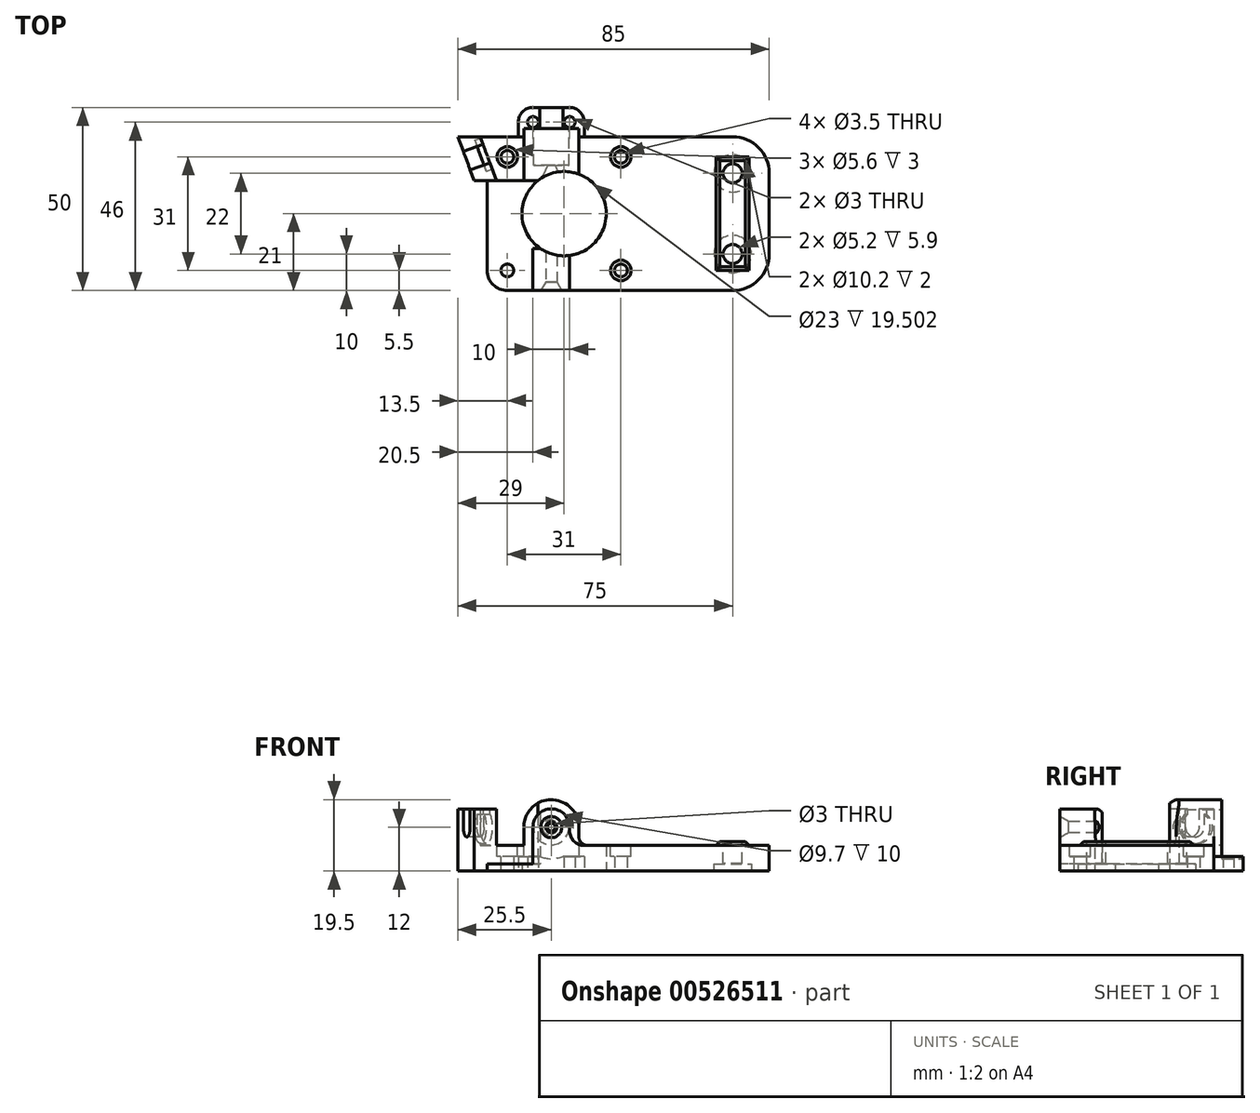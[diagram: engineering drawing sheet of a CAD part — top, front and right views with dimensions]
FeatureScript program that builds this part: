
annotation { "Feature Type Name" : "Feature", "Feature Type Description" : "" }
export const myFeature = defineFeature(function(context is Context, id is Id, definition is map)
    precondition{}
    {
        {
            var Q0;
            Q0=qCreatedBy(makeId("Top.planeOp"),FACE);
            var sketch = newSketch(context, id + "F0", { "sketchPlane" : qUnion([Q0])});
            skLineSegment(sketch, "E0.bottom", {"start": v(42.5, -21) * mm, "end": v(-34.5, -21) * mm});
            skLineSegment(sketch, "E0.top", {"start": v(42.5, 21) * mm, "end": v(-42.5, 21) * mm});
            skLineSegment(sketch, "E0.left", {"start": v(42.5, -21) * mm, "end": v(42.5, 21) * mm});
            skPoint(sketch, "E0.middle", {"position": v(0, 0) * mm});
            skLineSegment(sketch, "E1", {"start": v(-42.5, 21) * mm, "end": v(-38.06, 9) * mm});
            skLineSegment(sketch, "E2", {"start": v(-38.06, 9) * mm, "end": v(-34.5, 9) * mm});
            skLineSegment(sketch, "E3", {"start": v(-34.5, 9) * mm, "end": v(-34.5, -21) * mm});
            skPoint(sketch, "E4.orphan", {"position": v(-42.5, -21) * mm});
            skSolve(sketch);
        }
        {
            var Q0;
            Q0=makeQuery(id+"F0.imprint","IMPRINT",FACE,{"disambiguationData":[TD([[makeQuery(id+"F0.imprint","IMPRINT",EDGE,{"derivedFrom":sQuery(id+"F0.wireOp",EDGE,"E0.bottom")}),-1.0]])]});
            extrude(context, id + "F1", {"entities" : qUnion([Q0]), "depth" : 7 * mm, "offsetDistance" : 25 * mm});
        }
        {
            var Q0;
            Q0=makeQuery(id+"F1.opExtrude","SWEPT_FACE",FACE,{"disambiguationData":[OSD([sQuery(id+"F0.wireOp",EDGE,"E0.bottom")])]});
            var Q1;
            Q1=makeQuery(id+"F1.opExtrude","SWEPT_FACE",FACE,{"disambiguationData":[OSD([sQuery(id+"F0.wireOp",EDGE,"E0.top")])]});
            cPlane(context, id + "F2", {"entities" : qUnion([Q0, Q1]), "cplaneType" : CPlaneType.MID_PLANE, "offset" : 25 * mm, "width" : 150 * mm, "height" : 150 * mm});
        }
        {
            var Q0;
            Q0=makeQuery(id+"F1.opExtrude","SWEPT_FACE",FACE,{"disambiguationData":[OSD([sQuery(id+"F0.wireOp",EDGE,"E0.bottom")])]});
            var sketch = newSketch(context, id + "F3", { "sketchPlane" : qUnion([Q0])});
            skLineSegment(sketch, "E5", {"start": v(-22, 0) * mm, "end": v(-22, 12) * mm});
            skArc(sketch, "E6", {"start": v(-22, 12) * mm, "mid": v(-17, 17) * mm, "end": v(-12, 12) * mm});
            skLineSegment(sketch, "E7", {"start": v(-12, 12) * mm, "end": v(-12, 0) * mm});
            skLineSegment(sketch, "E8", {"start": v(-12, 0) * mm, "end": v(-22, 0) * mm});
            skSolve(sketch);
        }
        {
            var Q0;
            Q0 = qSketchRegion(id + "F3", true);
            var Q1;
            Q1=qCreatedBy(id+"F2.planeOp",FACE);
            extrude(context, id + "F4", {"entities" : qUnion([Q0]), "operationType" : NewBodyOperationType.ADD, "endBound" : BoundingType.UP_TO_SURFACE, "oppositeDirection" : true, "depth" : 25 * mm, "endBoundEntityFace" : qUnion([Q1]), "offsetDistance" : 25 * mm});
        }
        {
            var Q0;
            Q0=makeQuery(id+"F4.boolean.opBoolean","MERGE",FACE,{"derivedFrom":[makeQuery(id+"F1.opExtrude","SWEPT_FACE",FACE,{"disambiguationData":[OSD([sQuery(id+"F0.wireOp",EDGE,"E0.bottom")])]}),makeQuery(id+"F4.opExtrude","CAP_FACE",FACE,{"disambiguationData":[OSD([sQuery(id+"F3.wireOp",EDGE,"E5"),sQuery(id+"F3.wireOp",EDGE,"E6"),sQuery(id+"F3.wireOp",EDGE,"E7"),sQuery(id+"F3.wireOp",EDGE,"E8")])],"isStart":true})]});
            var sketch = newSketch(context, id + "F5", { "sketchPlane" : qUnion([Q0])});
            skPoint(sketch, "E9", {"position": v(-17, 12) * mm});
            skSolve(sketch);
        }
        {
            var Q0;
            Q0=sQuery(id+"F5.wireOp",VERTEX,"E9");
            var Q1;
            Q1=makeQuery(id+"F1.opExtrude","SWEPT_BODY",BODY,{"disambiguationData":[OSD([sQuery(id+"F0.wireOp",EDGE,"E0.bottom"),sQuery(id+"F0.wireOp",EDGE,"E0.top"),sQuery(id+"F0.wireOp",EDGE,"E0.left"),sQuery(id+"F0.wireOp",EDGE,"E1"),sQuery(id+"F0.wireOp",EDGE,"E2"),sQuery(id+"F0.wireOp",EDGE,"E3")])]});
            hole(context, id + "F6", {"style" : HoleStyle.C_SINK, "endStyle" : HoleEndStyle.THROUGH, "standardTappedOrClearance" : lookupTablePath({ "standard" : "ISO", "size" : "3", "type" : "Drilled" }), "standardBlindInLast" : lookupTablePath({ "standard" : "ISO", "size" : "3", "type" : "Drilled" }), "holeDiameter" : 3 * mm, "cSinkDiameter" : 5.76 * mm, "cSinkAngle" : 60 * degree, "isTappedThrough" : true, "tappedDepth" : 12 * mm, "tapClearance" : 3, "locations" : qUnion([Q0]), "scope" : qUnion([Q1])});
        }
        {
            var Q0;
            Q0=qCreatedBy(id+"F2.planeOp",FACE);
            var sketch = newSketch(context, id + "F7", { "sketchPlane" : qUnion([Q0])});
            skLineSegment(sketch, "E10", {"start": v(-24.5, 0) * mm, "end": v(-24.5, 12) * mm});
            skArc(sketch, "E11", {"start": v(-24.5, 12) * mm, "mid": v(-17, 19.5) * mm, "end": v(-9.5, 12) * mm});
            skLineSegment(sketch, "E12", {"start": v(-9.5, 12) * mm, "end": v(-9.5, 0) * mm});
            skLineSegment(sketch, "E13", {"start": v(-9.5, 0) * mm, "end": v(-24.5, 0) * mm});
            skSolve(sketch);
        }
        {
            var Q0;
            Q0=makeQuery(id+"F7.imprint","IMPRINT",FACE,{"disambiguationData":[TD([[makeQuery(id+"F7.imprint","IMPRINT",EDGE,{"derivedFrom":sQuery(id+"F7.wireOp",EDGE,"E10")}),-1.0]])]});
            var Q1;
            Q1=sQuery(id+"F7.wireOp",EDGE,"E11");
            extrude(context, id + "F8", {"entities" : qUnion([Q0]), "operationType" : NewBodyOperationType.ADD, "surfaceEntities" : qUnion([Q1]), "oppositeDirection" : true, "depth" : 23.2 * mm, "offsetDistance" : 25 * mm});
        }
        {
            var Q0;
            Q0=makeQuery(id+"F8.boolean.opBoolean","MERGE",FACE,{"derivedFrom":[makeQuery(id+"F1.opExtrude","CAP_FACE",FACE,{"disambiguationData":[OSD([sQuery(id+"F0.wireOp",EDGE,"E0.bottom"),sQuery(id+"F0.wireOp",EDGE,"E0.top"),sQuery(id+"F0.wireOp",EDGE,"E0.left"),sQuery(id+"F0.wireOp",EDGE,"E1"),sQuery(id+"F0.wireOp",EDGE,"E2"),sQuery(id+"F0.wireOp",EDGE,"E3")])],"isStart":true}),makeQuery(id+"F8.opExtrude","SWEPT_FACE",FACE,{"disambiguationData":[OSD([sQuery(id+"F7.wireOp",EDGE,"E13")])]})]});
            var sketch = newSketch(context, id + "F9", { "sketchPlane" : qUnion([Q0])});
            skLineSegment(sketch, "E14", {"start": v(-8, -21) * mm, "end": v(-8, -29) * mm});
            skLineSegment(sketch, "E15", {"start": v(-8, -29) * mm, "end": v(-26, -29) * mm});
            skLineSegment(sketch, "E16", {"start": v(-26, -29) * mm, "end": v(-26, -21) * mm});
            skLineSegment(sketch, "E17", {"start": v(-8, -21) * mm, "end": v(-26, -21) * mm});
            skCircle(sketch, "E18", {"center": v(-12, -25) * mm, "radius": 1.5 * mm});
            skCircle(sketch, "E19", {"center": v(-22, -25) * mm, "radius": 1.5 * mm});
            skLineSegment(sketch, "E20", {"start": v(-12, -25) * mm, "end": v(-22, -25) * mm, "construction": true});
            skLineSegment(sketch, "E21", {"start": v(-17, -29) * mm, "end": v(-17, -25) * mm, "construction": true});
            skSolve(sketch);
        }
        {
            var Q0;
            {var subQ4=sQuery(id+"F9.wireOp",EDGE,"E14");Q0=makeQuery(id+"F9.imprint","IMPRINT",FACE,{"disambiguationData":[TD([[makeQuery(id+"F9.imprint","IMPRINT",EDGE,{"derivedFrom":subQ4}),-1.0]])]});}
            extrude(context, id + "F10", {"entities" : qUnion([Q0]), "operationType" : NewBodyOperationType.ADD, "oppositeDirection" : true, "depth" : 4 * mm, "offsetDistance" : 25 * mm});
        }
        {
            var Q0;
            Q0=makeQuery(id+"F10.opExtrude","SWEPT_FACE",FACE,{"disambiguationData":[OSD([sQuery(id+"F9.wireOp",EDGE,"E15")])]});
            var sketch = newSketch(context, id + "F11", { "sketchPlane" : qUnion([Q0])});
            skCircle(sketch, "E22", {"center": v(17, 12) * mm, "radius": 8.6 * mm});
            skSolve(sketch);
        }
        {
            var Q0;
            Q0 = qSketchRegion(id + "F11", true);
            var Q1;
            Q1=makeQuery(id+"F8.opExtrude","CAP_FACE",FACE,{"disambiguationData":[OSD([sQuery(id+"F7.wireOp",EDGE,"E10"),sQuery(id+"F7.wireOp",EDGE,"E11"),sQuery(id+"F7.wireOp",EDGE,"E12"),sQuery(id+"F7.wireOp",EDGE,"E13")])],"isStart":false});
            extrude(context, id + "F12", {"entities" : qUnion([Q0]), "operationType" : NewBodyOperationType.REMOVE, "endBound" : BoundingType.UP_TO_SURFACE, "oppositeDirection" : true, "depth" : 25 * mm, "endBoundEntityFace" : qUnion([Q1]), "offsetDistance" : 25 * mm});
        }
        {
            var Q0;
            {var subQ0=sQuery(id+"F7.wireOp",EDGE,"E13");var subQ1=sQuery(id+"F7.wireOp",EDGE,"E12");var subQ2=sQuery(id+"F7.wireOp",EDGE,"E11");var subQ3=sQuery(id+"F7.wireOp",EDGE,"E10");Q0=makeQuery(id+"F12.boolean.opBoolean","MERGE",FACE,{"derivedFrom":[makeQuery(id+"F8.opExtrude","CAP_FACE",FACE,{"disambiguationData":[OSD([subQ3,subQ2,subQ1,subQ0])],"isStart":false}),makeQuery(id+"F12.opExtrude","CAP_FACE",FACE,{"disambiguationData":[OSD([subQ3,subQ2,subQ1,subQ0])],"isStart":false})]});}
            var sketch = newSketch(context, id + "F13", { "sketchPlane" : qUnion([Q0])});
            skCircle(sketch, "E23", {"center": v(17, 12) * mm, "radius": 4.85 * mm});
            skSolve(sketch);
        }
        {
            var Q0;
            Q0 = qSketchRegion(id + "F13", true);
            extrude(context, id + "F14", {"entities" : qUnion([Q0]), "operationType" : NewBodyOperationType.REMOVE, "oppositeDirection" : true, "depth" : 10 * mm, "offsetDistance" : 25 * mm});
        }
        {
            var Q0;
            {var subQ0=sQuery(id+"F0.wireOp",EDGE,"E2");var subQ2=sQuery(id+"F0.wireOp",EDGE,"E0.top");var subQ4=sQuery(id+"F0.wireOp",EDGE,"E1");var subQ5=sQuery(id+"F0.wireOp",EDGE,"E0.bottom");var subQ6=sQuery(id+"F0.wireOp",EDGE,"E3");Q0=makeQuery(id+"F8.boolean.opBoolean","SPLIT",FACE,{"disambiguationData":[TD([makeQuery(id+"F1.opExtrude","SWEPT_FACE",FACE,{"disambiguationData":[OSD([subQ4])]})])],"derivedFrom":makeQuery(id+"F1.opExtrude","CAP_FACE",FACE,{"disambiguationData":[OSD([subQ5,subQ2,sQuery(id+"F0.wireOp",EDGE,"E0.left"),subQ4,subQ0,subQ6])],"isStart":false})});}
            var sketch = newSketch(context, id + "F15", { "sketchPlane" : qUnion([Q0])});
            skLineSegment(sketch, "E24", {"start": v(-42.5, 21) * mm, "end": v(-36.42, 21) * mm});
            skLineSegment(sketch, "E25", {"start": v(-36.42, 21) * mm, "end": v(-31.98, 9) * mm});
            skLineSegment(sketch, "E26", {"start": v(-31.98, 9) * mm, "end": v(-38.06, 9) * mm});
            skLineSegment(sketch, "E27", {"start": v(-38.06, 9) * mm, "end": v(-42.5, 21) * mm});
            skSolve(sketch);
        }
        {
            var Q0;
            Q0 = qSketchRegion(id + "F15", true);
            extrude(context, id + "F16", {"entities" : qUnion([Q0]), "operationType" : NewBodyOperationType.ADD, "depth" : 10 * mm, "offsetDistance" : 25 * mm});
        }
        {
            var Q0;
            Q0=makeQuery(id+"F16.boolean.opBoolean","MERGE",FACE,{"derivedFrom":[makeQuery(id+"F1.opExtrude","SWEPT_FACE",FACE,{"disambiguationData":[OSD([sQuery(id+"F0.wireOp",EDGE,"E1")])]}),makeQuery(id+"F16.opExtrude","SWEPT_FACE",FACE,{"disambiguationData":[OSD([sQuery(id+"F15.wireOp",EDGE,"E27")])]})]});
            var sketch = newSketch(context, id + "F17", { "sketchPlane" : qUnion([Q0])});
            skLineSegment(sketch, "E28", {"start": v(-30.14, 17) * mm, "end": v(-30.14, 12) * mm});
            skArc(sketch, "E29", {"start": v(-30.14, 12) * mm, "mid": v(-27.44, 9.3) * mm, "end": v(-24.74, 12) * mm});
            skLineSegment(sketch, "E30", {"start": v(-24.74, 12) * mm, "end": v(-24.74, 17) * mm});
            skLineSegment(sketch, "E31", {"start": v(-30.14, 17) * mm, "end": v(-24.74, 17) * mm});
            skSolve(sketch);
        }
        {
            var Q0;
            Q0 = qSketchRegion(id + "F17", true);
            extrude(context, id + "F18", {"entities" : qUnion([Q0]), "operationType" : NewBodyOperationType.REMOVE, "endBound" : BoundingType.UP_TO_NEXT, "oppositeDirection" : true, "depth" : 25 * mm, "offsetDistance" : 25 * mm});
        }
        {
            var Q0;
            Q0=makeQuery(id+"F16.opExtrude","SWEPT_FACE",FACE,{"disambiguationData":[OSD([sQuery(id+"F15.wireOp",EDGE,"E25")])]});
            var sketch = newSketch(context, id + "F19", { "sketchPlane" : qUnion([Q0])});
            skCircle(sketch, "E32", {"center": v(27.44, 12) * mm, "radius": 4.5 * mm});
            skSolve(sketch);
        }
        {
            var Q0;
            Q0 = qSketchRegion(id + "F19", true);
            var Q1;
            Q1=makeQuery(id+"F16.boolean.opBoolean","MERGE",FACE,{"derivedFrom":[makeQuery(id+"F1.opExtrude","SWEPT_FACE",FACE,{"disambiguationData":[OSD([sQuery(id+"F0.wireOp",EDGE,"E1")])]}),makeQuery(id+"F16.opExtrude","SWEPT_FACE",FACE,{"disambiguationData":[OSD([sQuery(id+"F15.wireOp",EDGE,"E27")])]})]});
            extrude(context, id + "F20", {"entities" : qUnion([Q0]), "operationType" : NewBodyOperationType.REMOVE, "endBound" : BoundingType.UP_TO_SURFACE, "oppositeDirection" : true, "depth" : .5 * mm, "endBoundEntityFace" : qUnion([Q1]), "hasOffset" : true, "offsetDistance" : 4 * mm});
        }
        {
            var Q0;
            {var subQ1=sQuery(id+"F0.wireOp",EDGE,"E0.left");var subQ2=sQuery(id+"F0.wireOp",EDGE,"E0.top");var subQ4=sQuery(id+"F0.wireOp",EDGE,"E0.bottom");Q0=makeQuery(id+"F8.boolean.opBoolean","SPLIT",FACE,{"disambiguationData":[TD([makeQuery(id+"F1.opExtrude","SWEPT_FACE",FACE,{"disambiguationData":[OSD([subQ1])]})])],"derivedFrom":makeQuery(id+"F1.opExtrude","CAP_FACE",FACE,{"disambiguationData":[OSD([subQ4,subQ2,subQ1,sQuery(id+"F0.wireOp",EDGE,"E1"),sQuery(id+"F0.wireOp",EDGE,"E2"),sQuery(id+"F0.wireOp",EDGE,"E3")])],"isStart":false})});}
            var sketch = newSketch(context, id + "F21", { "sketchPlane" : qUnion([Q0])});
            skLineSegment(sketch, "E33.bottom", {"start": v(37, -15.5) * mm, "end": v(28, -15.5) * mm});
            skLineSegment(sketch, "E33.top", {"start": v(37, 15.5) * mm, "end": v(28, 15.5) * mm});
            skLineSegment(sketch, "E33.left", {"start": v(37, -15.5) * mm, "end": v(37, 15.5) * mm});
            skLineSegment(sketch, "E33.right", {"start": v(28, -15.5) * mm, "end": v(28, 15.5) * mm});
            skPoint(sketch, "E33.middle", {"position": v(32.5, 0) * mm});
            skSolve(sketch);
        }
        {
            var Q0;
            Q0 = qSketchRegion(id + "F21", true);
            extrude(context, id + "F22", {"entities" : qUnion([Q0]), "operationType" : NewBodyOperationType.ADD, "depth" : 1 * mm, "offsetDistance" : 25 * mm});
        }
        {
            var Q0;
            Q0=makeQuery(id+"F22.opExtrude","CAP_EDGE",EDGE,{"disambiguationData":[OSD([sQuery(id+"F21.wireOp",EDGE,"E33.left")])],"isStart":false});
            var Q1;
            Q1=makeQuery(id+"F22.opExtrude","CAP_EDGE",EDGE,{"disambiguationData":[OSD([sQuery(id+"F21.wireOp",EDGE,"E33.top")])],"isStart":false});
            var Q2;
            Q2=makeQuery(id+"F22.opExtrude","CAP_EDGE",EDGE,{"disambiguationData":[OSD([sQuery(id+"F21.wireOp",EDGE,"E33.right")])],"isStart":false});
            var Q3;
            Q3=makeQuery(id+"F22.opExtrude","CAP_EDGE",EDGE,{"disambiguationData":[OSD([sQuery(id+"F21.wireOp",EDGE,"E33.bottom")])],"isStart":false});
            chamfer(context, id + "F23", {"entities" : qUnion([Q0, Q1, Q2, Q3]), "width" : 1 * mm, "tangentPropagation" : true});
        }
        {
            var Q0;
            Q0=makeQuery(id+"F22.opExtrude","CAP_FACE",FACE,{"disambiguationData":[OSD([sQuery(id+"F21.wireOp",EDGE,"E33.bottom"),sQuery(id+"F21.wireOp",EDGE,"E33.top"),sQuery(id+"F21.wireOp",EDGE,"E33.left"),sQuery(id+"F21.wireOp",EDGE,"E33.right")])],"isStart":false});
            var sketch = newSketch(context, id + "F24", { "sketchPlane" : qUnion([Q0])});
            skCircle(sketch, "E34", {"center": v(32.5, -11) * mm, "radius": 2.6 * mm});
            skPoint(sketch, "E34.centerSnap0", {"position": v(32.5, -14.5) * mm});
            skCircle(sketch, "E35", {"center": v(32.5, 11) * mm, "radius": 2.6 * mm});
            skLineSegment(sketch, "E36", {"start": v(32.5, -11) * mm, "end": v(32.5, 11) * mm, "construction": true});
            skLineSegment(sketch, "E37", {"start": v(36, 0) * mm, "end": v(32.5, 0) * mm, "construction": true});
            skSolve(sketch);
        }
        {
            var Q0;
            Q0 = qSketchRegion(id + "F24", true);
            extrude(context, id + "F25", {"entities" : qUnion([Q0]), "operationType" : NewBodyOperationType.REMOVE, "oppositeDirection" : true, "depth" : 5.9 * mm, "offsetDistance" : 25 * mm});
        }
        {
            var Q0;
            {var subQ0=sQuery(id+"F7.wireOp",EDGE,"E13");Q0=makeQuery(id+"F10.boolean.opBoolean","MERGE",FACE,{"derivedFrom":[makeQuery(id+"F8.boolean.opBoolean","MERGE",FACE,{"derivedFrom":[makeQuery(id+"F1.opExtrude","CAP_FACE",FACE,{"disambiguationData":[OSD([sQuery(id+"F0.wireOp",EDGE,"E0.bottom"),sQuery(id+"F0.wireOp",EDGE,"E0.top"),sQuery(id+"F0.wireOp",EDGE,"E0.left"),sQuery(id+"F0.wireOp",EDGE,"E1"),sQuery(id+"F0.wireOp",EDGE,"E2"),sQuery(id+"F0.wireOp",EDGE,"E3")])],"isStart":true}),makeQuery(id+"F8.opExtrude","SWEPT_FACE",FACE,{"disambiguationData":[OSD([subQ0])]})]}),makeQuery(id+"F10.opExtrude","CAP_FACE",FACE,{"disambiguationData":[OSD([sQuery(id+"F7.wireOp",EDGE,"E10"),sQuery(id+"F7.wireOp",EDGE,"E12"),subQ0,sQuery(id+"F9.wireOp",EDGE,"E14"),sQuery(id+"F9.wireOp",EDGE,"E15"),sQuery(id+"F9.wireOp",EDGE,"E16"),sQuery(id+"F9.wireOp",EDGE,"E17"),sQuery(id+"F9.wireOp",EDGE,"E18"),sQuery(id+"F9.wireOp",EDGE,"E19")])],"isStart":true})]});}
            var sketch = newSketch(context, id + "F26", { "sketchPlane" : qUnion([Q0])});
            skCircle(sketch, "E38", {"center": v(32.5, -11) * mm, "radius": 5.1 * mm});
            skCircle(sketch, "E39", {"center": v(32.5, 11) * mm, "radius": 5.1 * mm});
            skSolve(sketch);
        }
        {
            var Q0;
            Q0 = qSketchRegion(id + "F26", true);
            extrude(context, id + "F27", {"entities" : qUnion([Q0]), "operationType" : NewBodyOperationType.REMOVE, "oppositeDirection" : true, "depth" : 2 * mm, "offsetDistance" : 25 * mm});
        }
        {
            var Q0;
            {var subQ0=sQuery(id+"F7.wireOp",EDGE,"E13");Q0=makeQuery(id+"F10.boolean.opBoolean","MERGE",FACE,{"derivedFrom":[makeQuery(id+"F8.boolean.opBoolean","MERGE",FACE,{"derivedFrom":[makeQuery(id+"F1.opExtrude","CAP_FACE",FACE,{"disambiguationData":[OSD([sQuery(id+"F0.wireOp",EDGE,"E0.bottom"),sQuery(id+"F0.wireOp",EDGE,"E0.top"),sQuery(id+"F0.wireOp",EDGE,"E0.left"),sQuery(id+"F0.wireOp",EDGE,"E1"),sQuery(id+"F0.wireOp",EDGE,"E2"),sQuery(id+"F0.wireOp",EDGE,"E3")])],"isStart":true}),makeQuery(id+"F8.opExtrude","SWEPT_FACE",FACE,{"disambiguationData":[OSD([subQ0])]})]}),makeQuery(id+"F10.opExtrude","CAP_FACE",FACE,{"disambiguationData":[OSD([sQuery(id+"F7.wireOp",EDGE,"E10"),sQuery(id+"F7.wireOp",EDGE,"E12"),subQ0,sQuery(id+"F9.wireOp",EDGE,"E14"),sQuery(id+"F9.wireOp",EDGE,"E15"),sQuery(id+"F9.wireOp",EDGE,"E16"),sQuery(id+"F9.wireOp",EDGE,"E17"),sQuery(id+"F9.wireOp",EDGE,"E18"),sQuery(id+"F9.wireOp",EDGE,"E19")])],"isStart":true})]});}
            var sketch = newSketch(context, id + "F28", { "sketchPlane" : qUnion([Q0])});
            skLineSegment(sketch, "E40.bottom", {"start": v(2, -15.5) * mm, "end": v(-29, -15.5) * mm, "construction": true});
            skLineSegment(sketch, "E40.top", {"start": v(2, 15.5) * mm, "end": v(-29, 15.5) * mm, "construction": true});
            skLineSegment(sketch, "E40.left", {"start": v(2, -15.5) * mm, "end": v(2, 15.5) * mm, "construction": true});
            skLineSegment(sketch, "E40.right", {"start": v(-29, -15.5) * mm, "end": v(-29, 15.5) * mm, "construction": true});
            skPoint(sketch, "E40.middle", {"position": v(-13.5, 0) * mm});
            skPoint(sketch, "E41", {"position": v(2, -15.5) * mm});
            skPoint(sketch, "E42", {"position": v(-29, -15.5) * mm});
            skPoint(sketch, "E43", {"position": v(-29, 15.5) * mm});
            skPoint(sketch, "E44", {"position": v(2, 15.5) * mm});
            skSolve(sketch);
        }
        {
            var Q0;
            Q0=sQuery(id+"F28.wireOp",VERTEX,"E41");
            var Q1;
            Q1=sQuery(id+"F28.wireOp",VERTEX,"E42");
            var Q2;
            Q2=sQuery(id+"F28.wireOp",VERTEX,"E43");
            var Q3;
            Q3=sQuery(id+"F28.wireOp",VERTEX,"E44");
            var Q4;
            Q4=makeQuery(id+"F1.opExtrude","SWEPT_BODY",BODY,{"disambiguationData":[OSD([sQuery(id+"F0.wireOp",EDGE,"E0.bottom"),sQuery(id+"F0.wireOp",EDGE,"E0.top"),sQuery(id+"F0.wireOp",EDGE,"E0.left"),sQuery(id+"F0.wireOp",EDGE,"E1"),sQuery(id+"F0.wireOp",EDGE,"E2"),sQuery(id+"F0.wireOp",EDGE,"E3")])]});
            hole(context, id + "F29", {"style" : HoleStyle.SIMPLE, "endStyle" : HoleEndStyle.THROUGH, "standardTappedOrClearance" : lookupTablePath({ "standard" : "ISO", "size" : "3.5", "type" : "Drilled" }), "standardBlindInLast" : lookupTablePath({ "standard" : "ISO", "size" : "3.5", "type" : "Drilled" }), "holeDiameter" : 3.5 * mm, "isTappedThrough" : true, "tappedDepth" : 12 * mm, "tapClearance" : 3, "locations" : qUnion([Q0, Q1, Q2, Q3]), "scope" : qUnion([Q4])});
        }
        {
            var Q0;
            {var subQ1=sQuery(id+"F0.wireOp",EDGE,"E0.left");Q0=makeQuery(id+"F28.imprint","IMPRINT",FACE,{"disambiguationData":[TD([[makeQuery(id+"F28.imprint","IMPRINT",EDGE,{"derivedFrom":makeQuery(id+"F1.opExtrude","CAP_EDGE",EDGE,{"disambiguationData":[OSD([subQ1])],"isStart":true})}),-1.0]])]});}
            var sketch = newSketch(context, id + "F30", { "sketchPlane" : qUnion([Q0])});
            skCircle(sketch, "E45", {"center": v(-13.5, 0) * mm, "radius": 11.5 * mm});
            skSolve(sketch);
        }
        {
            var Q0;
            Q0 = qSketchRegion(id + "F30", true);
            extrude(context, id + "F31", {"entities" : qUnion([Q0]), "operationType" : NewBodyOperationType.REMOVE, "endBound" : BoundingType.UP_TO_NEXT, "oppositeDirection" : true, "depth" : 25 * mm, "offsetDistance" : 25 * mm});
        }
        {
            var Q0;
            {var subQ0=sQuery(id+"F0.wireOp",EDGE,"E2");var subQ2=sQuery(id+"F0.wireOp",EDGE,"E0.top");var subQ4=sQuery(id+"F0.wireOp",EDGE,"E1");var subQ5=sQuery(id+"F0.wireOp",EDGE,"E0.bottom");var subQ6=sQuery(id+"F0.wireOp",EDGE,"E3");Q0=makeQuery(id+"F8.boolean.opBoolean","SPLIT",FACE,{"disambiguationData":[TD([makeQuery(id+"F1.opExtrude","SWEPT_FACE",FACE,{"disambiguationData":[OSD([subQ4])]})])],"derivedFrom":makeQuery(id+"F1.opExtrude","CAP_FACE",FACE,{"disambiguationData":[OSD([subQ5,subQ2,sQuery(id+"F0.wireOp",EDGE,"E0.left"),subQ4,subQ0,subQ6])],"isStart":false})});}
            var sketch = newSketch(context, id + "F32", { "sketchPlane" : qUnion([Q0])});
            skLineSegment(sketch, "E46", {"start": v(-34.5, -21) * mm, "end": v(-22, -21) * mm});
            skLineSegment(sketch, "E47", {"start": v(-22, -21) * mm, "end": v(-22, -9.5) * mm});
            skLineSegment(sketch, "E48", {"start": v(-22, -9.5) * mm, "end": v(-13.5, -9.5) * mm});
            skLineSegment(sketch, "E49", {"start": v(-13.5, -9.5) * mm, "end": v(-13.5, 9) * mm});
            skLineSegment(sketch, "E50", {"start": v(-13.5, 9) * mm, "end": v(-34.5, 9) * mm});
            skLineSegment(sketch, "E51", {"start": v(-34.5, 9) * mm, "end": v(-34.5, -21) * mm});
            skSolve(sketch);
        }
        {
            var Q0;
            Q0 = qSketchRegion(id + "F32", true);
            var Q1;
            {var subQ0=sQuery(id+"F7.wireOp",EDGE,"E13");Q1=makeQuery(id+"F10.boolean.opBoolean","MERGE",FACE,{"derivedFrom":[makeQuery(id+"F8.boolean.opBoolean","MERGE",FACE,{"derivedFrom":[makeQuery(id+"F1.opExtrude","CAP_FACE",FACE,{"disambiguationData":[OSD([sQuery(id+"F0.wireOp",EDGE,"E0.bottom"),sQuery(id+"F0.wireOp",EDGE,"E0.top"),sQuery(id+"F0.wireOp",EDGE,"E0.left"),sQuery(id+"F0.wireOp",EDGE,"E1"),sQuery(id+"F0.wireOp",EDGE,"E2"),sQuery(id+"F0.wireOp",EDGE,"E3")])],"isStart":true}),makeQuery(id+"F8.opExtrude","SWEPT_FACE",FACE,{"disambiguationData":[OSD([subQ0])]})]}),makeQuery(id+"F10.opExtrude","CAP_FACE",FACE,{"disambiguationData":[OSD([sQuery(id+"F7.wireOp",EDGE,"E10"),sQuery(id+"F7.wireOp",EDGE,"E12"),subQ0,sQuery(id+"F9.wireOp",EDGE,"E14"),sQuery(id+"F9.wireOp",EDGE,"E15"),sQuery(id+"F9.wireOp",EDGE,"E16"),sQuery(id+"F9.wireOp",EDGE,"E17"),sQuery(id+"F9.wireOp",EDGE,"E18"),sQuery(id+"F9.wireOp",EDGE,"E19")])],"isStart":true})]});}
            extrude(context, id + "F33", {"entities" : qUnion([Q0]), "operationType" : NewBodyOperationType.REMOVE, "endBound" : BoundingType.UP_TO_SURFACE, "oppositeDirection" : true, "depth" : 25 * mm, "endBoundEntityFace" : qUnion([Q1]), "hasOffset" : true, "offsetDistance" : 2 * mm, "hasSecondDirection" : true, "secondDirectionBound" : BoundingType.THROUGH_ALL, "secondDirectionOppositeDirection" : false, "secondDirectionDepth" : 25 * mm});
        }
        {
            var Q0;
            Q0=makeQuery(id+"F14.boolean.opBoolean","COPY",FACE,{"derivedFrom":makeQuery(id+"F14.opExtrude","CAP_FACE",FACE,{"disambiguationData":[OSD([sQuery(id+"F13.wireOp",EDGE,"E23")])],"isStart":false})});
            var sketch = newSketch(context, id + "F34", { "sketchPlane" : qUnion([Q0])});
            skCircle(sketch, "E52", {"center": v(17, 12) * mm, "radius": 1.05 * mm});
            skSolve(sketch);
        }
        {
            var Q0;
            Q0=makeQuery(id+"F34.imprint","IMPRINT",FACE,{"disambiguationData":[TD([[makeQuery(id+"F34.imprint","IMPRINT",EDGE,{"derivedFrom":sQuery(id+"F34.wireOp",EDGE,"E52")}),1.0]])]});
            extrude(context, id + "F35", {"entities" : qUnion([Q0]), "operationType" : NewBodyOperationType.REMOVE, "endBound" : BoundingType.UP_TO_NEXT, "oppositeDirection" : true, "depth" : 25 * mm, "offsetDistance" : 25 * mm, "hasDraft" : true, "draftAngle" : 22.6 * degree});
        }
        {
            var Q0;
            {var subQ1=sQuery(id+"F0.wireOp",EDGE,"E0.left");var subQ2=sQuery(id+"F0.wireOp",EDGE,"E0.top");var subQ4=sQuery(id+"F0.wireOp",EDGE,"E0.bottom");Q0=makeQuery(id+"F8.boolean.opBoolean","SPLIT",FACE,{"disambiguationData":[TD([makeQuery(id+"F1.opExtrude","SWEPT_FACE",FACE,{"disambiguationData":[OSD([subQ1])]})])],"derivedFrom":makeQuery(id+"F1.opExtrude","CAP_FACE",FACE,{"disambiguationData":[OSD([subQ4,subQ2,subQ1,sQuery(id+"F0.wireOp",EDGE,"E1"),sQuery(id+"F0.wireOp",EDGE,"E2"),sQuery(id+"F0.wireOp",EDGE,"E3")])],"isStart":false})});}
            var sketch = newSketch(context, id + "F36", { "sketchPlane" : qUnion([Q0])});
            skCircle(sketch, "E53", {"center": v(2, -15.5) * mm, "radius": 2.8 * mm});
            skCircle(sketch, "E54", {"center": v(2, 15.5) * mm, "radius": 2.8 * mm});
            skCircle(sketch, "E55", {"center": v(-29, 15.5) * mm, "radius": 2.8 * mm});
            skSolve(sketch);
        }
        {
            var Q0;
            Q0 = qSketchRegion(id + "F36", true);
            extrude(context, id + "F37", {"entities" : qUnion([Q0]), "operationType" : NewBodyOperationType.REMOVE, "oppositeDirection" : true, "depth" : 3 * mm, "offsetDistance" : 25 * mm});
        }
        {
            var Q0;
            Q0=makeQuery(id+"F4.boolean.opBoolean","INTERSECT",EDGE,{"derivedFrom":[makeQuery(id+"F1.opExtrude","CAP_FACE",FACE,{"disambiguationData":[OSD([sQuery(id+"F0.wireOp",EDGE,"E0.bottom"),sQuery(id+"F0.wireOp",EDGE,"E0.top"),sQuery(id+"F0.wireOp",EDGE,"E0.left"),sQuery(id+"F0.wireOp",EDGE,"E1"),sQuery(id+"F0.wireOp",EDGE,"E2"),sQuery(id+"F0.wireOp",EDGE,"E3")])],"isStart":false}),makeQuery(id+"F4.opExtrude","SWEPT_FACE",FACE,{"disambiguationData":[OSD([sQuery(id+"F3.wireOp",EDGE,"E7")])]})]});
            var Q1;
            Q1=makeQuery(id+"F10.opExtrude","SWEPT_EDGE",EDGE,{"disambiguationData":[OSD([sQuery(id+"F9.wireOp",EDGE,"E14"),sQuery(id+"F9.wireOp",EDGE,"E15")])]});
            var Q2;
            Q2=makeQuery(id+"F10.opExtrude","SWEPT_EDGE",EDGE,{"disambiguationData":[OSD([sQuery(id+"F9.wireOp",EDGE,"E15"),sQuery(id+"F9.wireOp",EDGE,"E16")])]});
            fillet(context, id + "F38", {"entities" : qUnion([Q0, Q1, Q2]), "radius" : 4 * mm, "tangentPropagation" : true, "allowEdgeOverflow" : false});
        }
        {
            var Q0;
            Q0=makeQuery(id+"F1.opExtrude","SWEPT_EDGE",EDGE,{"disambiguationData":[OSD([sQuery(id+"F0.wireOp",EDGE,"E0.bottom"),sQuery(id+"F0.wireOp",EDGE,"E3")])]});
            fillet(context, id + "F39", {"entities" : qUnion([Q0]), "radius" : 5.5 * mm, "tangentPropagation" : true, "allowEdgeOverflow" : false});
        }
        {
            var Q0;
            Q0=makeQuery(id+"F8.boolean.opBoolean","INTERSECT",EDGE,{"derivedFrom":[makeQuery(id+"F1.opExtrude","CAP_FACE",FACE,{"disambiguationData":[OSD([sQuery(id+"F0.wireOp",EDGE,"E0.bottom"),sQuery(id+"F0.wireOp",EDGE,"E0.top"),sQuery(id+"F0.wireOp",EDGE,"E0.left"),sQuery(id+"F0.wireOp",EDGE,"E1"),sQuery(id+"F0.wireOp",EDGE,"E2"),sQuery(id+"F0.wireOp",EDGE,"E3")])],"isStart":false}),makeQuery(id+"F8.opExtrude","SWEPT_FACE",FACE,{"disambiguationData":[OSD([sQuery(id+"F7.wireOp",EDGE,"E12")])]})]});
            fillet(context, id + "F40", {"entities" : qUnion([Q0]), "radius" : 2.5 * mm, "tangentPropagation" : true, "allowEdgeOverflow" : false});
        }
        {
            var Q0;
            Q0=makeQuery(id+"F1.opExtrude","SWEPT_EDGE",EDGE,{"disambiguationData":[OSD([sQuery(id+"F0.wireOp",EDGE,"E0.top"),sQuery(id+"F0.wireOp",EDGE,"E0.left")])]});
            var Q1;
            Q1=makeQuery(id+"F1.opExtrude","SWEPT_EDGE",EDGE,{"disambiguationData":[OSD([sQuery(id+"F0.wireOp",EDGE,"E0.bottom"),sQuery(id+"F0.wireOp",EDGE,"E0.left")])]});
            fillet(context, id + "F41", {"entities" : qUnion([Q0, Q1]), "radius" : 10 * mm, "tangentPropagation" : true, "allowEdgeOverflow" : false});
        }
    });
